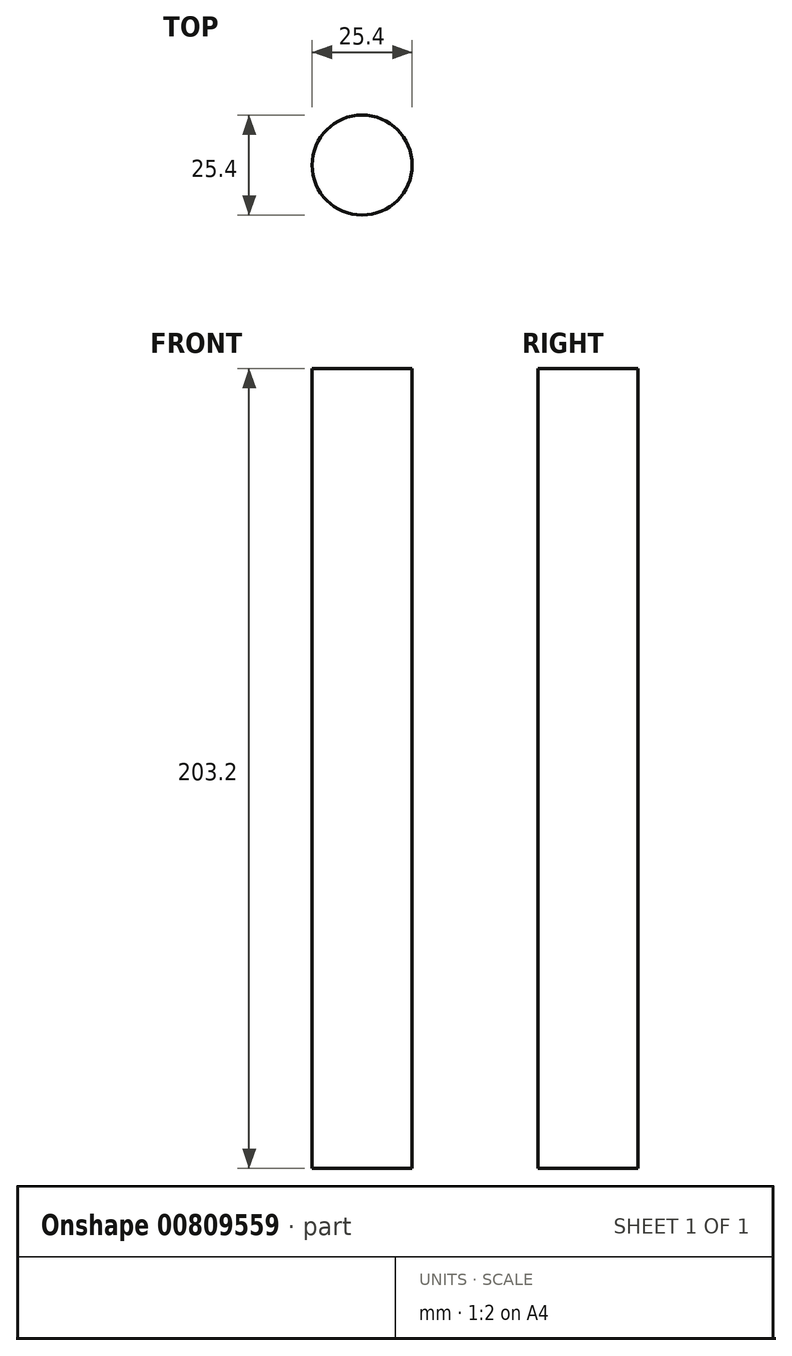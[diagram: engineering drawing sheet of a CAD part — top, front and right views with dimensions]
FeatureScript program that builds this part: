
annotation { "Feature Type Name" : "Feature", "Feature Type Description" : "" }
export const myFeature = defineFeature(function(context is Context, id is Id, definition is map)
    precondition{}
    {
        {
            var Q0;
            Q0=qCreatedBy(makeId("Top.planeOp"),FACE);
            var sketch = newSketch(context, id + "F0", { "sketchPlane" : qUnion([Q0])});
            skCircle(sketch, "E0", {"center": v(0, 0) * mm, "radius": 12.7 * mm});
            skSolve(sketch);
        }
        {
            var Q0;
            Q0=qSketchRegion(id+"F0",true);
            var Q1;
            Q1=makeQuery(id+"F0.imprint","IMPRINT",FACE,{"disambiguationData":[TD([[makeQuery(id+"F0.imprint","IMPRINT",EDGE,{"derivedFrom":sQuery(id+"F0.wireOp",EDGE,"E0")}),1.0]])]});
            extrude(context, id + "F1", {"entities" : qUnion([Q0, Q1]), "depth" : 203.2 * mm, "offsetDistance" : 25.4 * mm});
        }
    });
